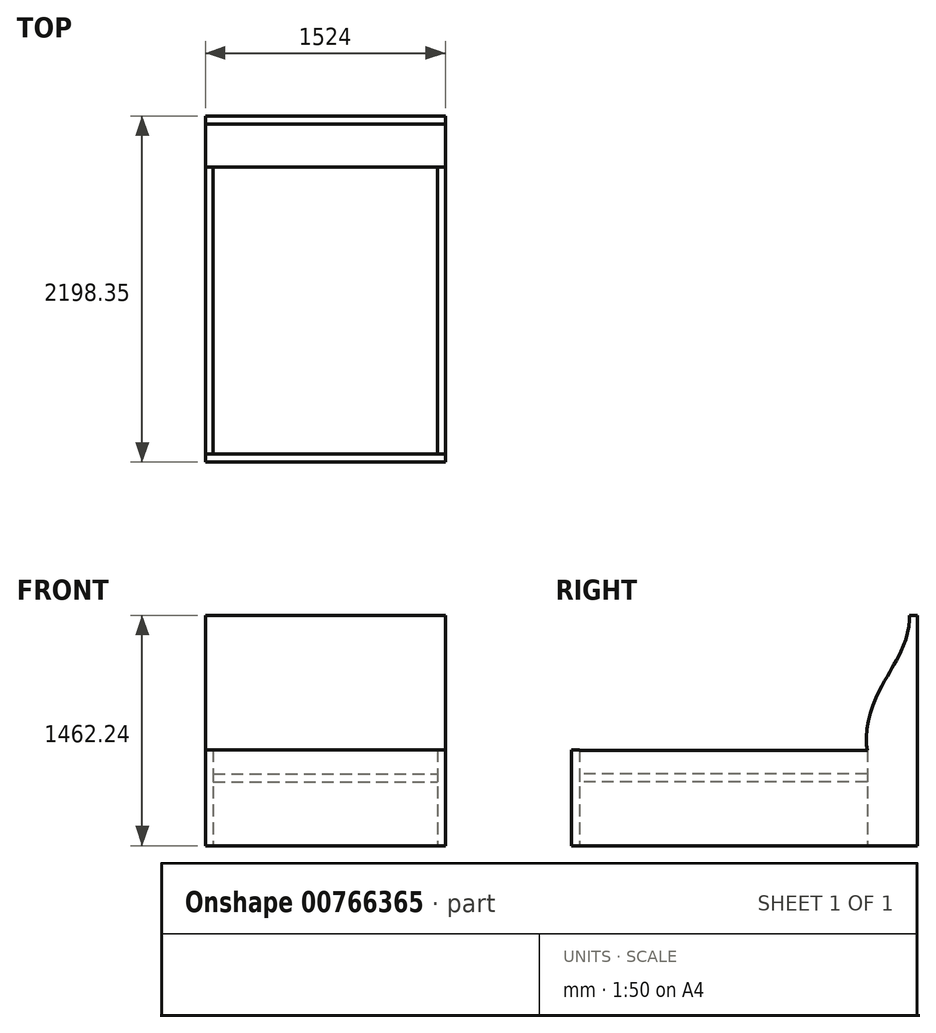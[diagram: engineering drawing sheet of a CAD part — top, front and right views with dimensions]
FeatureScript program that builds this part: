
annotation { "Feature Type Name" : "Feature", "Feature Type Description" : "" }
export const myFeature = defineFeature(function(context is Context, id is Id, definition is map)
    precondition{}
    {
        {
            var Q0;
            Q0=qCreatedBy(makeId("Right.planeOp"),FACE);
            var sketch = newSketch(context, id + "F0", { "sketchPlane" : qUnion([Q0])});
            skFitSpline(sketch, "E0", {"points": [v(877.94, 852.64) * mm, v(761.27, 492.93) * mm, v(610, 0) * mm], "startDerivative": vector(0, -935.6) * mm, "endDerivative": vector(132.13, -1153.31) * mm});
            skLineSegment(sketch, "E1", {"start": v(610, 0) * mm, "end": v(610, -609.6) * mm});
            skLineSegment(sketch, "E2.0", {"start": v(559.2, -2.84) * mm, "end": v(559.2, -609.6) * mm});
            skFitSpline(sketch, "E2.1", {"points": [v(827.14, 852.64) * mm, v(827.14, 834.76) * mm, v(825.44, 800.69) * mm, v(818.34, 753.44) * mm, v(807.15, 708.86) * mm, v(792.18, 665.78) * mm, v(776.79, 630.28) * mm, v(762.87, 601.68) * mm, v(751.69, 580.03) * mm, v(739.8, 558.08) * mm, v(729.37, 539.46) * mm, v(720.72, 524.31) * mm, v(711.9, 509) * mm, v(700.53, 489.43) * mm, v(686.52, 465.27) * mm, v(672.31, 440.4) * mm, v(658.1, 414.76) * mm, v(639.36, 379.51) * mm, v(616.83, 333.35) * mm, v(592.73, 274.2) * mm, v(573.15, 210.94) * mm, v(559.72, 143.34) * mm, v(554.08, 71.32) * mm, v(556.52, 20.4) * mm, v(559.52, -5.78) * mm]});
            skLineSegment(sketch, "E3", {"start": v(827.14, 852.64) * mm, "end": v(877.94, 852.64) * mm});
            skLineSegment(sketch, "E4", {"start": v(610, -609.6) * mm, "end": v(559.2, -609.6) * mm});
            skLineSegment(sketch, "E5", {"start": v(877.94, 852.64) * mm, "end": v(877.94, -609.6) * mm});
            skLineSegment(sketch, "E6", {"start": v(877.94, -609.6) * mm, "end": v(610, -609.6) * mm});
            skSolve(sketch);
        }
        {
            var Q0;
            Q0=makeQuery(id+"F0.imprint","IMPRINT",FACE,{"disambiguationData":[TD([[makeQuery(id+"F0.imprint","IMPRINT",EDGE,{"derivedFrom":sQuery(id+"F0.wireOp",EDGE,"E0")}),-1.0]])]});
            var Q1;
            Q1=makeQuery(id+"F0.imprint","IMPRINT",FACE,{"disambiguationData":[TD([[makeQuery(id+"F0.imprint","IMPRINT",EDGE,{"derivedFrom":sQuery(id+"F0.wireOp",EDGE,"E0")}),1.0]])]});
            extrude(context, id + "F1", {"entities" : qUnion([Q0, Q1]), "oppositeDirection" : true, "depth" : 1524 * mm, "offsetDistance" : 25.4 * mm});
        }
        {
            var Q0;
            Q0=makeQuery(id+"F1.opExtrude","SWEPT_FACE",FACE,{"disambiguationData":[OSD([sQuery(id+"F0.wireOp",EDGE,"E2.0")])]});
            var sketch = newSketch(context, id + "F2", { "sketchPlane" : qUnion([Q0])});
            skLineSegment(sketch, "E7.bottom", {"start": v(0, 0) * mm, "end": v(-50.8, 0) * mm});
            skLineSegment(sketch, "E7.top", {"start": v(0, -609.6) * mm, "end": v(-50.8, -609.6) * mm});
            skLineSegment(sketch, "E7.left", {"start": v(0, 0) * mm, "end": v(0, -609.6) * mm});
            skLineSegment(sketch, "E7.right", {"start": v(-50.8, 0) * mm, "end": v(-50.8, -609.6) * mm});
            skLineSegment(sketch, "E8.bottom", {"start": v(-656.76, -26.46) * mm, "end": v(-968.53, -26.46) * mm});
            skLineSegment(sketch, "E8.top", {"start": v(-656.76, 195.14) * mm, "end": v(-968.53, 195.14) * mm});
            skLineSegment(sketch, "E8.left", {"start": v(-656.76, -26.46) * mm, "end": v(-656.76, 195.14) * mm});
            skLineSegment(sketch, "E8.right", {"start": v(-968.53, -26.46) * mm, "end": v(-968.53, 195.14) * mm});
            skLineSegment(sketch, "E9", {"start": v(-762, -609.6) * mm, "end": v(-762, -207.22) * mm, "construction": true});
            skLineSegment(sketch, "E10.MirrorCS", {"start": v(-1524, 0) * mm, "end": v(-1473.2, 0) * mm});
            skLineSegment(sketch, "E11.MirrorCS", {"start": v(-1524, -609.6) * mm, "end": v(-1473.2, -609.6) * mm});
            skLineSegment(sketch, "E12.MirrorCS", {"start": v(-1473.2, 0) * mm, "end": v(-1473.2, -609.6) * mm});
            skLineSegment(sketch, "E13.MirrorCS", {"start": v(-1524, 0) * mm, "end": v(-1524, -609.6) * mm});
            skSolve(sketch);
        }
        {
            var Q0;
            {var subQ0=sQuery(id+"F2.wireOp",EDGE,"E7.top");Q0=makeQuery(id+"F2.imprint","IMPRINT",FACE,{"disambiguationData":[TD([[makeQuery(id+"F2.imprint","IMPRINT",EDGE,{"derivedFrom":subQ0}),1.0]])]});}
            var Q1;
            {var subQ0=sQuery(id+"F2.wireOp",EDGE,"E11.MirrorCS");Q1=makeQuery(id+"F2.imprint","IMPRINT",FACE,{"disambiguationData":[TD([[makeQuery(id+"F2.imprint","IMPRINT",EDGE,{"derivedFrom":subQ0}),1.0]])]});}
            extrude(context, id + "F3", {"entities" : qUnion([Q0, Q1]), "operationType" : NewBodyOperationType.ADD, "depth" : 1828.8 * mm, "offsetDistance" : 25.4 * mm});
        }
        {
            var Q0;
            Q0=makeQuery(id+"F3.opExtrude","CAP_FACE",FACE,{"disambiguationData":[OSD([sQuery(id+"F0.wireOp",EDGE,"E2.0"),sQuery(id+"F0.wireOp",EDGE,"E2.1"),sQuery(id+"F2.wireOp",EDGE,"E7.top"),sQuery(id+"F2.wireOp",EDGE,"E7.left"),sQuery(id+"F2.wireOp",EDGE,"E7.right")])],"isStart":false});
            var sketch = newSketch(context, id + "F4", { "sketchPlane" : qUnion([Q0])});
            skPoint(sketch, "E14.0", {"position": v(0, -2.84) * mm});
            skPoint(sketch, "E15.0", {"position": v(-1524, -609.6) * mm});
            skLineSegment(sketch, "E16.bottom", {"start": v(0, 0) * mm, "end": v(-1524, 0) * mm});
            skLineSegment(sketch, "E16.top", {"start": v(0, -609.6) * mm, "end": v(-1524, -609.6) * mm});
            skLineSegment(sketch, "E16.left", {"start": v(0, 0) * mm, "end": v(0, -609.6) * mm});
            skLineSegment(sketch, "E16.right", {"start": v(-1524, 0) * mm, "end": v(-1524, -609.6) * mm});
            skSolve(sketch);
        }
        {
            var Q0;
            {var subQ6=sQuery(id+"F4.wireOp",EDGE,"E16.bottom");Q0=makeQuery(id+"F4.imprint","IMPRINT",FACE,{"disambiguationData":[TD([[makeQuery(id+"F4.imprint","IMPRINT",EDGE,{"derivedFrom":subQ6}),1.0]])]});}
            var Q1;
            {var subQ3=sQuery(id+"F2.wireOp",EDGE,"E7.right");var subQ4=makeQuery(id+"F3.opExtrude","CAP_EDGE",EDGE,{"disambiguationData":[OSD([subQ3])],"isStart":false});Q1=makeQuery(id+"F4.imprint","IMPRINT",FACE,{"disambiguationData":[TD([[makeQuery(id+"F4.imprint","IMPRINT",EDGE,{"derivedFrom":subQ4}),1.0]])]});}
            extrude(context, id + "F5", {"entities" : qUnion([Q0, Q1]), "operationType" : NewBodyOperationType.ADD, "depth" : 50.8 * mm, "offsetDistance" : 25.4 * mm});
        }
        {
            var Q0;
            Q0=makeQuery(id+"F5.opExtrude","SWEPT_FACE",FACE,{"disambiguationData":[OSD([sQuery(id+"F4.wireOp",EDGE,"E16.bottom")])]});
            cPlane(context, id + "F6", {"entities" : qUnion([Q0]), "cplaneType" : CPlaneType.OFFSET, "offset" : 203.2 * mm, "oppositeDirection" : true, "width" : 152.4 * mm, "height" : 152.4 * mm});
        }
        {
            var Q0;
            Q0=qCreatedBy(id+"F6.planeOp",FACE);
            var sketch = newSketch(context, id + "F7", { "sketchPlane" : qUnion([Q0])});
            skPoint(sketch, "E17.0", {"position": v(-50.8, -1269.6) * mm});
            skPoint(sketch, "E18.0", {"position": v(-1473.2, 559.2) * mm});
            skLineSegment(sketch, "E19.bottom", {"start": v(-1473.2, 559.2) * mm, "end": v(-50.8, 559.2) * mm});
            skLineSegment(sketch, "E19.top", {"start": v(-1473.2, -1269.6) * mm, "end": v(-50.8, -1269.6) * mm});
            skLineSegment(sketch, "E19.left", {"start": v(-1473.2, 559.2) * mm, "end": v(-1473.2, -1269.6) * mm});
            skLineSegment(sketch, "E19.right", {"start": v(-50.8, 559.2) * mm, "end": v(-50.8, -1269.6) * mm});
            skSolve(sketch);
        }
        {
            var Q0;
            Q0=makeQuery(id+"F7.imprint","IMPRINT",FACE,{"disambiguationData":[TD([[makeQuery(id+"F7.imprint","IMPRINT",EDGE,{"derivedFrom":sQuery(id+"F7.wireOp",EDGE,"E19.bottom")}),-1.0]])]});
            extrude(context, id + "F8", {"entities" : qUnion([Q0]), "depth" : 50.8 * mm, "offsetDistance" : 25.4 * mm});
        }
    });
